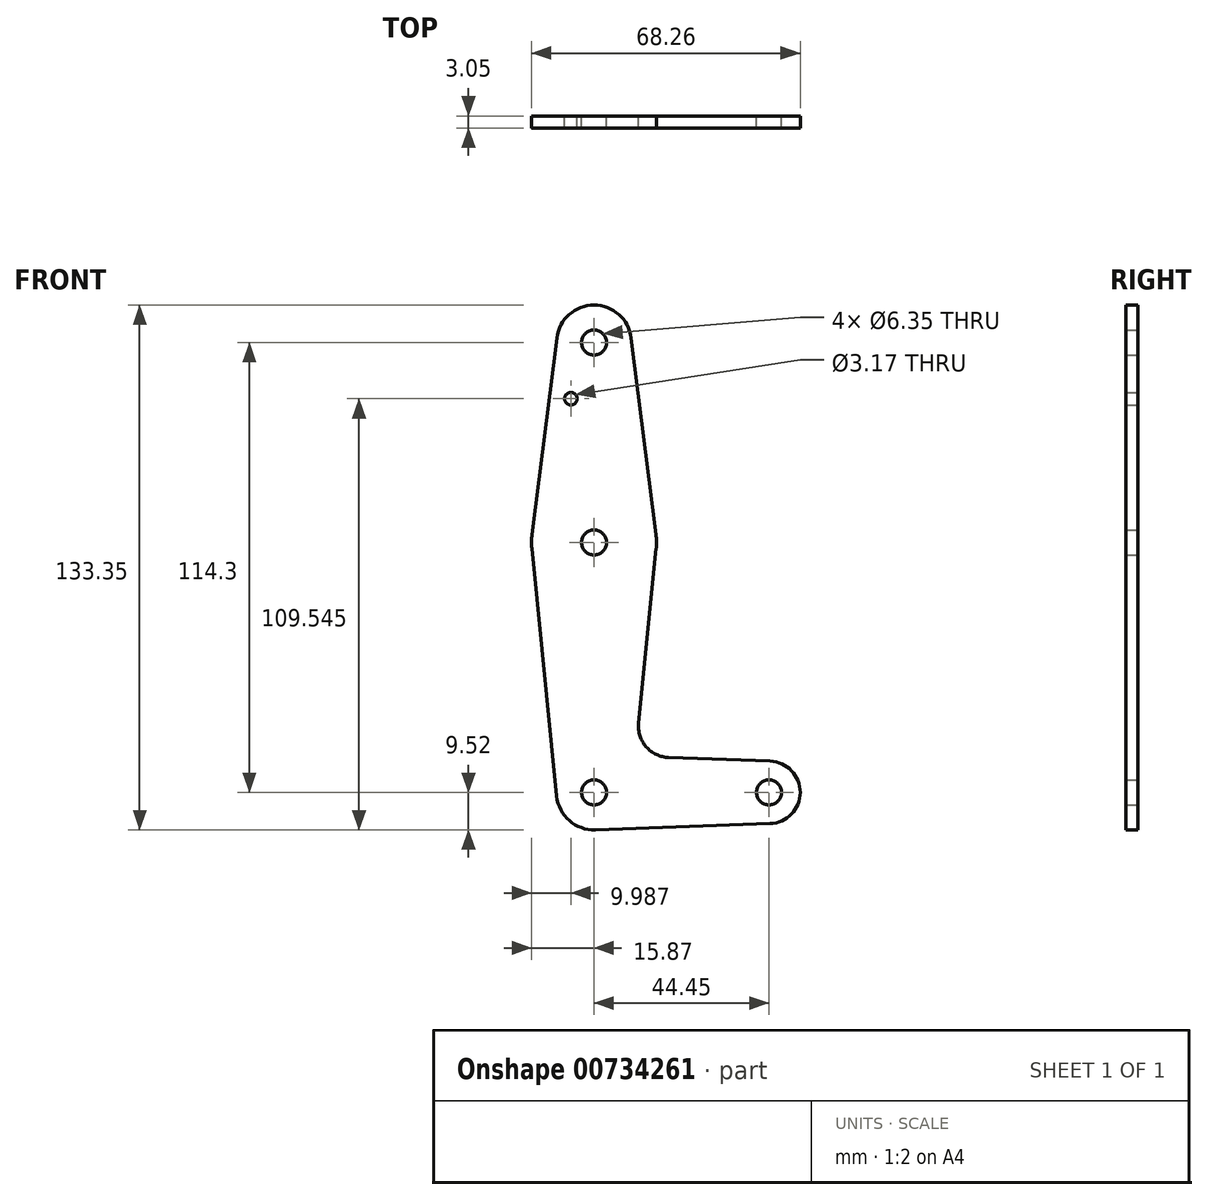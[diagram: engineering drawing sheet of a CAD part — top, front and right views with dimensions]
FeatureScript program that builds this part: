
annotation { "Feature Type Name" : "Feature", "Feature Type Description" : "" }
export const myFeature = defineFeature(function(context is Context, id is Id, definition is map)
    precondition{}
    {
        {
            var Q0;
            Q0=qCreatedBy(makeId("Front.planeOp"),FACE);
            var sketch = newSketch(context, id + "F0", { "sketchPlane" : qUnion([Q0])});
            skLineSegment(sketch, "E0", {"start": v(0, 0) * mm, "end": v(0, 114.3) * mm, "construction": true});
            skLineSegment(sketch, "E1", {"start": v(0, 0) * mm, "end": v(44.45, 0) * mm, "construction": true});
            skCircle(sketch, "E2", {"center": v(0, 114.3) * mm, "radius": 9.53 * mm});
            skCircle(sketch, "E3", {"center": v(0, 63.5) * mm, "radius": 15.88 * mm});
            skCircle(sketch, "E4", {"center": v(0, 0) * mm, "radius": 9.53 * mm});
            skCircle(sketch, "E5", {"center": v(44.45, 0) * mm, "radius": 7.94 * mm});
            skLineSegment(sketch, "E6", {"start": v(9.45, 115.5) * mm, "end": v(15.75, 65.48) * mm});
            skLineSegment(sketch, "E7", {"start": v(-9.45, 115.5) * mm, "end": v(-15.75, 65.48) * mm});
            skLineSegment(sketch, "E8", {"start": v(-15.8, 61.91) * mm, "end": v(-9.48, -0.95) * mm});
            skLineSegment(sketch, "E9", {"start": v(15.8, 61.91) * mm, "end": v(11.34, 17.6) * mm});
            skLineSegment(sketch, "E10", {"start": v(0.34, -9.52) * mm, "end": v(44.73, -7.93) * mm});
            skLineSegment(sketch, "E11", {"start": v(18.97, 8.85) * mm, "end": v(44.73, 7.93) * mm});
            skCircle(sketch, "E12", {"center": v(0, 114.3) * mm, "radius": 3.18 * mm});
            skCircle(sketch, "E13", {"center": v(0, 63.5) * mm, "radius": 3.18 * mm});
            skCircle(sketch, "E14", {"center": v(0, 0) * mm, "radius": 3.18 * mm});
            skCircle(sketch, "E15", {"center": v(44.45, 0) * mm, "radius": 3.18 * mm});
            skCircle(sketch, "E16", {"center": v(-5.88, 100.03) * mm, "radius": 1.59 * mm});
            skArc(sketch, "E17.filletArc", {"start": v(11.34, 17.6) * mm, "mid": v(13.26, 11.57) * mm, "end": v(18.97, 8.85) * mm});
            skSolve(sketch);
        }
        {
            var Q0;
            Q0 = qSketchRegion(id + "F0", true);
            extrude(context, id + "F1", {"entities" : qUnion([Q0]), "depth" : 3.05 * mm, "offsetDistance" : 25.4 * mm});
        }
    });
